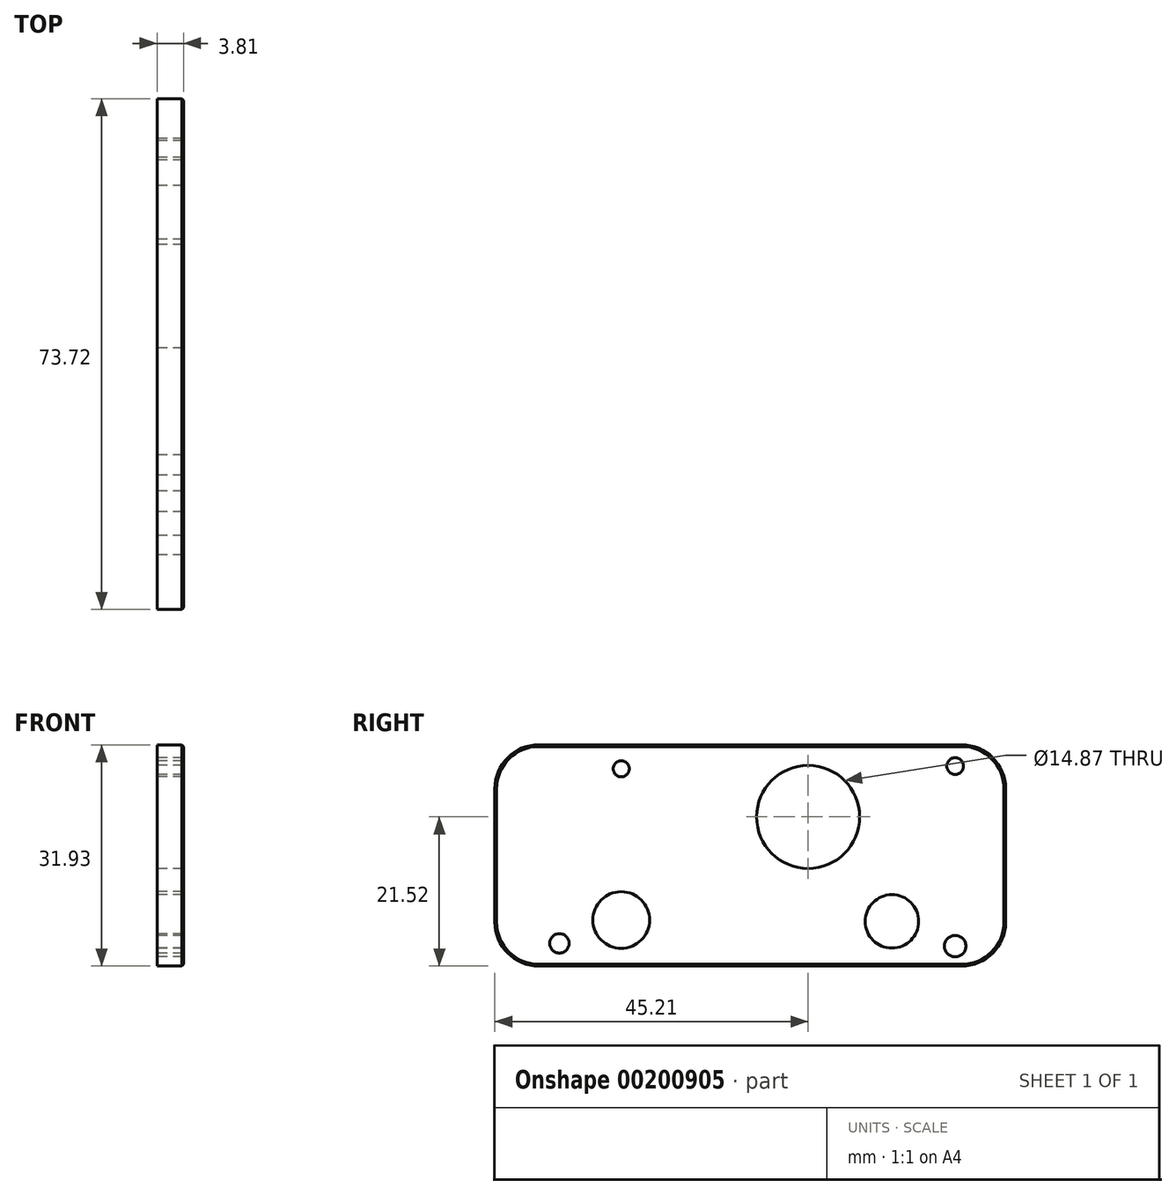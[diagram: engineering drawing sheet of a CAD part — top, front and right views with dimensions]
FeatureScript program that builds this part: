
annotation { "Feature Type Name" : "Feature", "Feature Type Description" : "" }
export const myFeature = defineFeature(function(context is Context, id is Id, definition is map)
    precondition{}
    {
        {
            var Q0;
            Q0=qCreatedBy(makeId("Right.planeOp"),FACE);
            var sketch = newSketch(context, id + "F0", { "sketchPlane" : qUnion([Q0])});
            skLineSegment(sketch, "E0", {"start": v(6.35, 0) * mm, "end": v(67.37, 0) * mm});
            skLineSegment(sketch, "E1", {"start": v(73.72, -6.35) * mm, "end": v(73.72, -25.58) * mm});
            skLineSegment(sketch, "E2", {"start": v(67.37, -31.93) * mm, "end": v(16.59, -31.93) * mm});
            skLineSegment(sketch, "E3", {"start": v(16.59, -31.93) * mm, "end": v(6.35, -31.93) * mm});
            skLineSegment(sketch, "E4", {"start": v(0, -6.35) * mm, "end": v(0, -25.58) * mm});
            skPoint(sketch, "E5.visualSharp", {"position": v(0, 0) * mm});
            skArc(sketch, "E5.filletArc", {"start": v(6.35, 0) * mm, "mid": v(1.86, -1.86) * mm, "end": v(0, -6.35) * mm});
            skPoint(sketch, "E6.visualSharp", {"position": v(73.72, 0) * mm});
            skArc(sketch, "E6.filletArc", {"start": v(73.72, -6.35) * mm, "mid": v(71.86, -1.86) * mm, "end": v(67.37, 0) * mm});
            skPoint(sketch, "E7.visualSharp", {"position": v(0, -31.93) * mm});
            skArc(sketch, "E7.filletArc", {"start": v(0, -25.58) * mm, "mid": v(1.86, -30.07) * mm, "end": v(6.35, -31.93) * mm});
            skPoint(sketch, "E8.visualSharp", {"position": v(73.72, -31.93) * mm});
            skArc(sketch, "E8.filletArc", {"start": v(67.37, -31.93) * mm, "mid": v(71.86, -30.07) * mm, "end": v(73.72, -25.58) * mm});
            skCircle(sketch, "E9", {"center": v(57.3, -25.48) * mm, "radius": 3.85 * mm});
            skCircle(sketch, "E10", {"center": v(18.24, -25.28) * mm, "radius": 4.09 * mm});
            skCircle(sketch, "E11", {"center": v(45.21, -10.41) * mm, "radius": 7.43 * mm});
            skCircle(sketch, "E12", {"center": v(45.21, -10.41) * mm, "radius": 6.26 * mm});
            skCircle(sketch, "E13", {"center": v(18.24, -3.47) * mm, "radius": 1.16 * mm});
            skCircle(sketch, "E14", {"center": v(9.32, -28.65) * mm, "radius": 1.4 * mm});
            skCircle(sketch, "E15", {"center": v(66.43, -29.05) * mm, "radius": 1.55 * mm});
            skCircle(sketch, "E16", {"center": v(66.43, -3.07) * mm, "radius": 1.2 * mm});
            skSolve(sketch);
        }
        {
            var Q0;
            Q0=makeQuery(id+"F0.imprint","IMPRINT",FACE,{"disambiguationData":[TD([[makeQuery(id+"F0.imprint","IMPRINT",EDGE,{"derivedFrom":sQuery(id+"F0.wireOp",EDGE,"E0")}),-1.0]])]});
            extrude(context, id + "F1", {"entities" : qUnion([Q0]), "depth" : 3.8 * mm});
        }
        {
            var Q0;
            Q0=makeQuery(id+"F1.opExtrude","CAP_EDGE",EDGE,{"disambiguationData":[OSD([sQuery(id+"F0.wireOp",EDGE,"E0")])],"isStart":false});
            var Q1;
            Q1=makeQuery(id+"F1.opExtrude","CAP_EDGE",EDGE,{"disambiguationData":[OSD([sQuery(id+"F0.wireOp",EDGE,"E5.filletArc")])],"isStart":false});
            var Q2;
            Q2=makeQuery(id+"F1.opExtrude","CAP_EDGE",EDGE,{"disambiguationData":[OSD([sQuery(id+"F0.wireOp",EDGE,"E4")])],"isStart":false});
            var Q3;
            Q3=makeQuery(id+"F1.opExtrude","CAP_EDGE",EDGE,{"disambiguationData":[OSD([sQuery(id+"F0.wireOp",EDGE,"E7.filletArc")])],"isStart":false});
            var Q4;
            Q4=makeQuery(id+"F1.opExtrude","CAP_EDGE",EDGE,{"disambiguationData":[OSD([sQuery(id+"F0.wireOp",EDGE,"E2"),sQuery(id+"F0.wireOp",EDGE,"E3")])],"isStart":false});
            var Q5;
            Q5=makeQuery(id+"F1.opExtrude","CAP_EDGE",EDGE,{"disambiguationData":[OSD([sQuery(id+"F0.wireOp",EDGE,"E8.filletArc")])],"isStart":false});
            var Q6;
            Q6=makeQuery(id+"F1.opExtrude","CAP_EDGE",EDGE,{"disambiguationData":[OSD([sQuery(id+"F0.wireOp",EDGE,"E1")])],"isStart":false});
            var Q7;
            Q7=makeQuery(id+"F1.opExtrude","CAP_EDGE",EDGE,{"disambiguationData":[OSD([sQuery(id+"F0.wireOp",EDGE,"E6.filletArc")])],"isStart":false});
            chamfer(context, id + "F2", {"entities" : qUnion([Q0, Q1, Q2, Q3, Q4, Q5, Q6, Q7]), "width" : 0.25 * mm, "tangentPropagation" : true});
        }
    });
